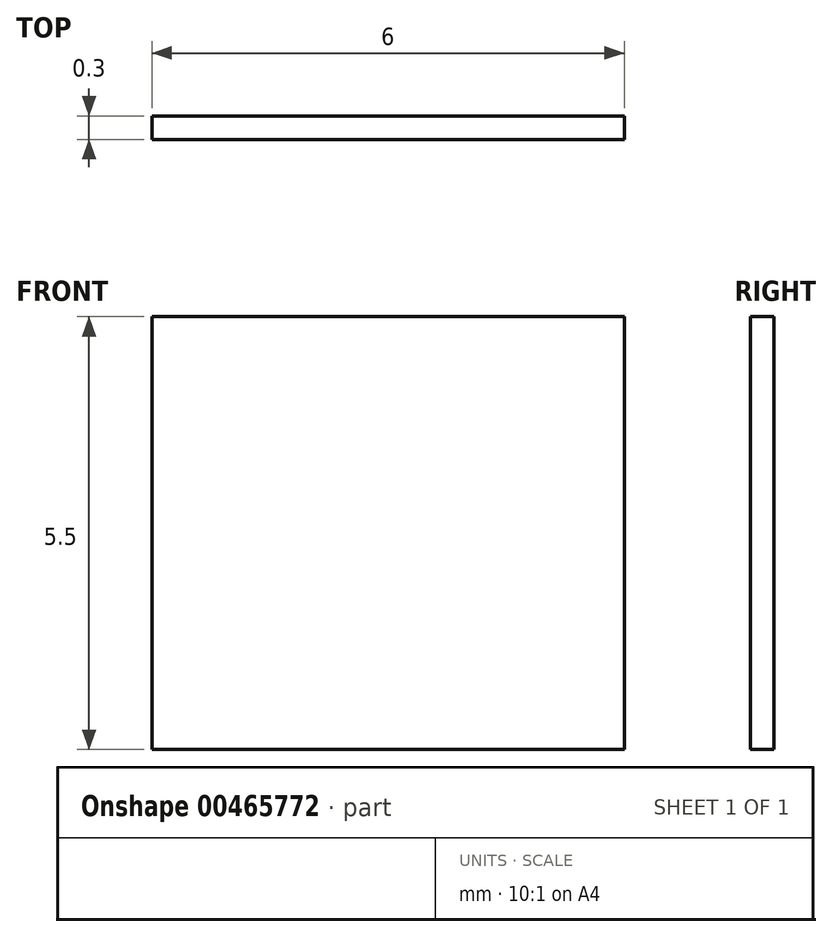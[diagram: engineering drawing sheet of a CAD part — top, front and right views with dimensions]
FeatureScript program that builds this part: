
annotation { "Feature Type Name" : "Feature", "Feature Type Description" : "" }
export const myFeature = defineFeature(function(context is Context, id is Id, definition is map)
    precondition{}
    {
        {
            var Q0;
            Q0=qCreatedBy(makeId("Front.planeOp"),FACE);
            var sketch = newSketch(context, id + "F0", { "sketchPlane" : qUnion([Q0])});
            skLineSegment(sketch, "E0.bottom", {"start": v(0, 0) * mm, "end": v(6, 0) * mm});
            skLineSegment(sketch, "E0.top", {"start": v(0, 5.5) * mm, "end": v(6, 5.5) * mm});
            skLineSegment(sketch, "E0.left", {"start": v(0, 0) * mm, "end": v(0, 5.5) * mm});
            skLineSegment(sketch, "E0.right", {"start": v(6, 0) * mm, "end": v(6, 5.5) * mm});
            skSolve(sketch);
        }
        {
            var Q0;
            Q0 = qSketchRegion(id + "F0", true);
            extrude(context, id + "F1", {"entities" : qUnion([Q0]), "depth" : 0.3 * mm});
        }
    });
